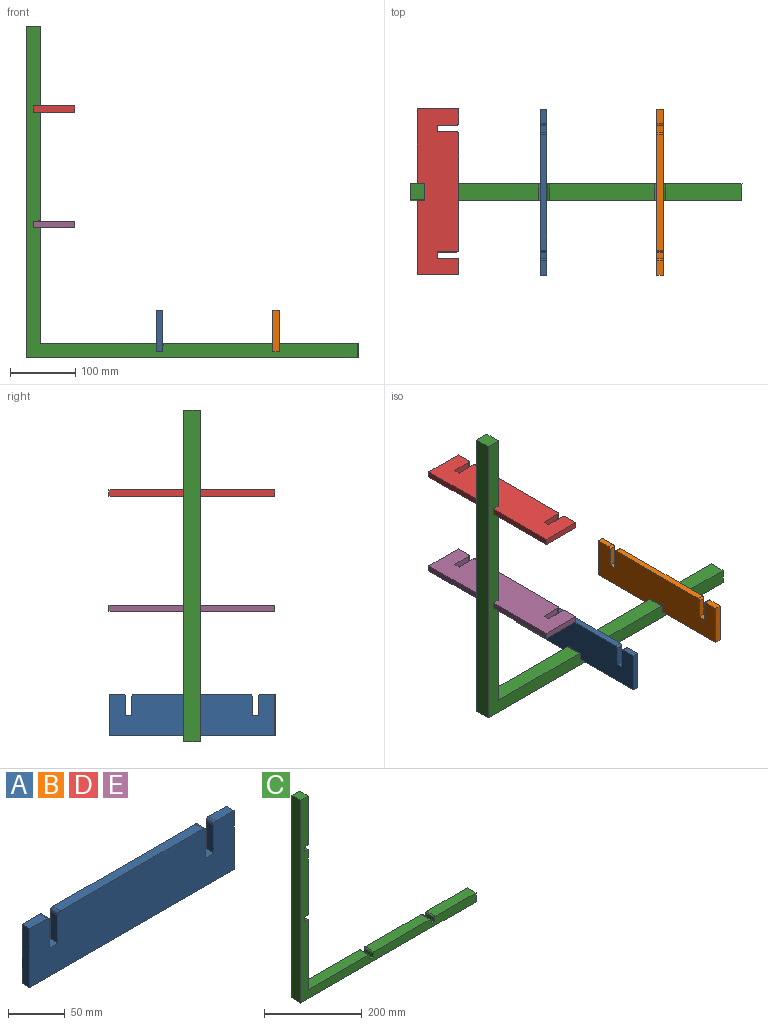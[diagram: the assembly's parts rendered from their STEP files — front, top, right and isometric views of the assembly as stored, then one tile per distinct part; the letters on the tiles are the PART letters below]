
ASSEMBLY  parts=5 mates=5
PART A: 18 faces, bbox 254x9.5x63.5 mm
  f0: cylinder r=3.17mm len=9.53mm, axis (0,1,0), area 47.5mm2, adj f1,f15,f16,f17
  f1: plane 29.86x9.53mm, normal (-1,0,0), area 284.5mm2, adj f0,f2,f16,f17
  f2: plane 9.91x9.53mm, normal (0,0,1), area 94.4mm2, adj f1,f3,f16,f17
  f3: plane 29.86x9.53mm, normal (1,0,0), area 284.5mm2, adj f2,f4,f16,f17
  f4: cylinder r=3.17mm len=9.53mm, axis (0,1,0), area 47.5mm2, adj f3,f5,f16,f17
  f5: plane 22.03x9.53mm, normal (0,0,1), area 209.9mm2, adj f4,f6,f16,f17
  f6: plane 63.5x9.53mm, normal (-1,0,0), area 604.8mm2, adj f5,f7,f16,f17
  f7: plane 254x9.53mm, normal (0,0,-1), area 2419.3mm2, adj f6,f8,f16,f17
  f8: plane 63.5x9.53mm, normal (1,0,0), area 604.8mm2, adj f7,f9,f16,f17
  f9: plane 22.03x9.53mm, normal (0,0,1), area 209.9mm2, adj f8,f10,f16,f17
  f10: cylinder r=3.17mm len=9.53mm, axis (0,1,0), area 47.5mm2, adj f9,f11,f16,f17
  f11: plane 29.86x9.53mm, normal (-1,0,0), area 284.5mm2, adj f10,f12,f16,f17
  f12: plane 9.91x9.53mm, normal (0,0,1), area 94.4mm2, adj f11,f13,f16,f17
  f13: plane 29.86x9.53mm, normal (1,0,0), area 284.5mm2, adj f12,f14,f16,f17
  f14: cylinder r=3.17mm len=9.53mm, axis (0,1,0), area 47.5mm2, adj f13,f15,f16,f17
  f15: plane 177.42x9.53mm, normal (0,0,1), area 1689.9mm2, adj f0,f14,f16,f17
  f16: plane 254x63.5mm, normal (0,-1,0), area 15465.8mm2, adj f0,f1,f2,f3,f4,f5,f6,f7
  f17: plane 254x63.5mm, normal (0,1,0), area 15465.8mm2, adj f0,f1,f2,f3,f4,f5,f6,f7
PART B: same geometry as A
PART C: 32 faces, bbox 508x25.4x508 mm
  f0: plane 25.4x9.53mm, normal (1,0,0), area 241.9mm2, adj f1,f29,f30,f31
  f1: plane 25.4x7.87mm, normal (0,0,-1), area 200mm2, adj f0,f2,f30,f31
  f2: cylinder r=3.17mm len=25.4mm, axis (0,1,0), area 126.7mm2, adj f1,f3,f30,f31
  f3: plane 160.27x25.4mm, normal (1,0,0), area 4071mm2, adj f2,f4,f30,f31
  f4: cylinder r=3.17mm len=25.4mm, axis (0,1,0), area 126.7mm2, adj f3,f5,f30,f31
  f5: plane 25.4x7.87mm, normal (0,0,1), area 200mm2, adj f4,f6,f30,f31
  f6: plane 25.4x9.53mm, normal (1,0,0), area 241.9mm2, adj f5,f7,f30,f31
  f7: plane 25.4x7.87mm, normal (0,0,-1), area 200mm2, adj f6,f8,f30,f31
  f8: cylinder r=3.17mm len=25.4mm, axis (0,1,0), area 126.7mm2, adj f7,f9,f30,f31
  f9: plane 119.13x25.4mm, normal (1,0,0), area 3025.8mm2, adj f8,f10,f30,f31
  f10: plane 25.4x22.23mm, normal (0,0,1), area 564.5mm2, adj f9,f11,f30,f31
  f11: plane 508x25.4mm, normal (-1,0,0), area 12903.2mm2, adj f10,f12,f30,f31
  f12: plane 508x25.4mm, normal (0,0,-1), area 12903.2mm2, adj f11,f13,f30,f31
  f13: plane 25.4x22.23mm, normal (1,0,0), area 564.5mm2, adj f12,f14,f30,f31
  f14: plane 117.48x25.4mm, normal (0,0,1), area 2983.9mm2, adj f13,f15,f30,f31
  f15: cylinder r=3.17mm len=25.4mm, axis (0,1,0), area 126.7mm2, adj f14,f16,f30,f31
  f16: plane 25.4x9.53mm, normal (-1,0,0), area 241.9mm2, adj f15,f17,f30,f31
  f17: plane 25.4x9.53mm, normal (0,0,1), area 241.9mm2, adj f16,f18,f30,f31
  f18: plane 25.4x9.53mm, normal (1,0,0), area 241.9mm2, adj f17,f19,f30,f31
  f19: cylinder r=3.17mm len=25.4mm, axis (0,1,0), area 126.7mm2, adj f18,f20,f30,f31
  f20: plane 161.93x25.4mm, normal (0,0,1), area 4112.9mm2, adj f19,f21,f30,f31
  f21: cylinder r=3.17mm len=25.4mm, axis (0,1,0), area 126.7mm2, adj f20,f22,f30,f31
  f22: plane 25.4x9.53mm, normal (-1,0,0), area 241.9mm2, adj f21,f23,f30,f31
  f23: plane 25.4x9.53mm, normal (0,0,1), area 241.9mm2, adj f22,f24,f30,f31
  f24: plane 25.4x9.53mm, normal (1,0,0), area 241.9mm2, adj f23,f25,f30,f31
  f25: cylinder r=3.17mm len=25.4mm, axis (0,1,0), area 126.7mm2, adj f24,f26,f30,f31
  f26: plane 174.63x25.4mm, normal (0,0,1), area 4435.5mm2, adj f25,f27,f30,f31
  f27: plane 174.63x25.4mm, normal (1,0,0), area 4435.5mm2, adj f26,f28,f30,f31
  f28: cylinder r=3.17mm len=25.4mm, axis (0,1,0), area 126.7mm2, adj f27,f29,f30,f31
  f29: plane 25.4x7.87mm, normal (0,0,1), area 200mm2, adj f0,f28,f30,f31
  f30: plane 508x508mm, normal (0,-1,0), area 21616.9mm2, adj f0,f1,f2,f3,f4,f5,f6,f7
  f31: plane 508x508mm, normal (0,1,0), area 21616.9mm2, adj f0,f1,f2,f3,f4,f5,f6,f7
PART D: same geometry as A
PART E: same geometry as A
PLACE A rot(axis=(0,0,1),90deg) t=(-386.72,-1.64,137.14)mm
PLACE B rot(axis=(0,0,1),90deg) t=(-208.92,-1.64,137.14)mm
PLACE C rot(axis=(0,0,-1),0deg) t=(-268.9,27.09,284.7)mm
PLACE D rot(axis=(0.58,0.58,0.58),120deg) t=(-512.07,-1.64,449.81)mm
PLACE E rot(axis=(0.58,0.58,0.58),120deg) t=(-512.07,-1.64,273.67)mm
MATE parallel D.f16 <-> C.f7  axis (0,0,-1) through (-575.57,14.39,440.29)mm
MATE planar D.f7 <-> C.f6  axis (-1,0,0) through (-575.57,14.39,445.05)mm
MATE planar A.f7 <-> C.f23  axis (0,0,-1) through (-381.95,14.39,73.64)mm
MATE planar B.f7 <-> C.f17  axis (0,0,-1) through (-204.15,14.39,73.64)mm
MATE planar E.f7 <-> C.f0  axis (-1,0,0) through (-575.57,14.39,268.9)mm
